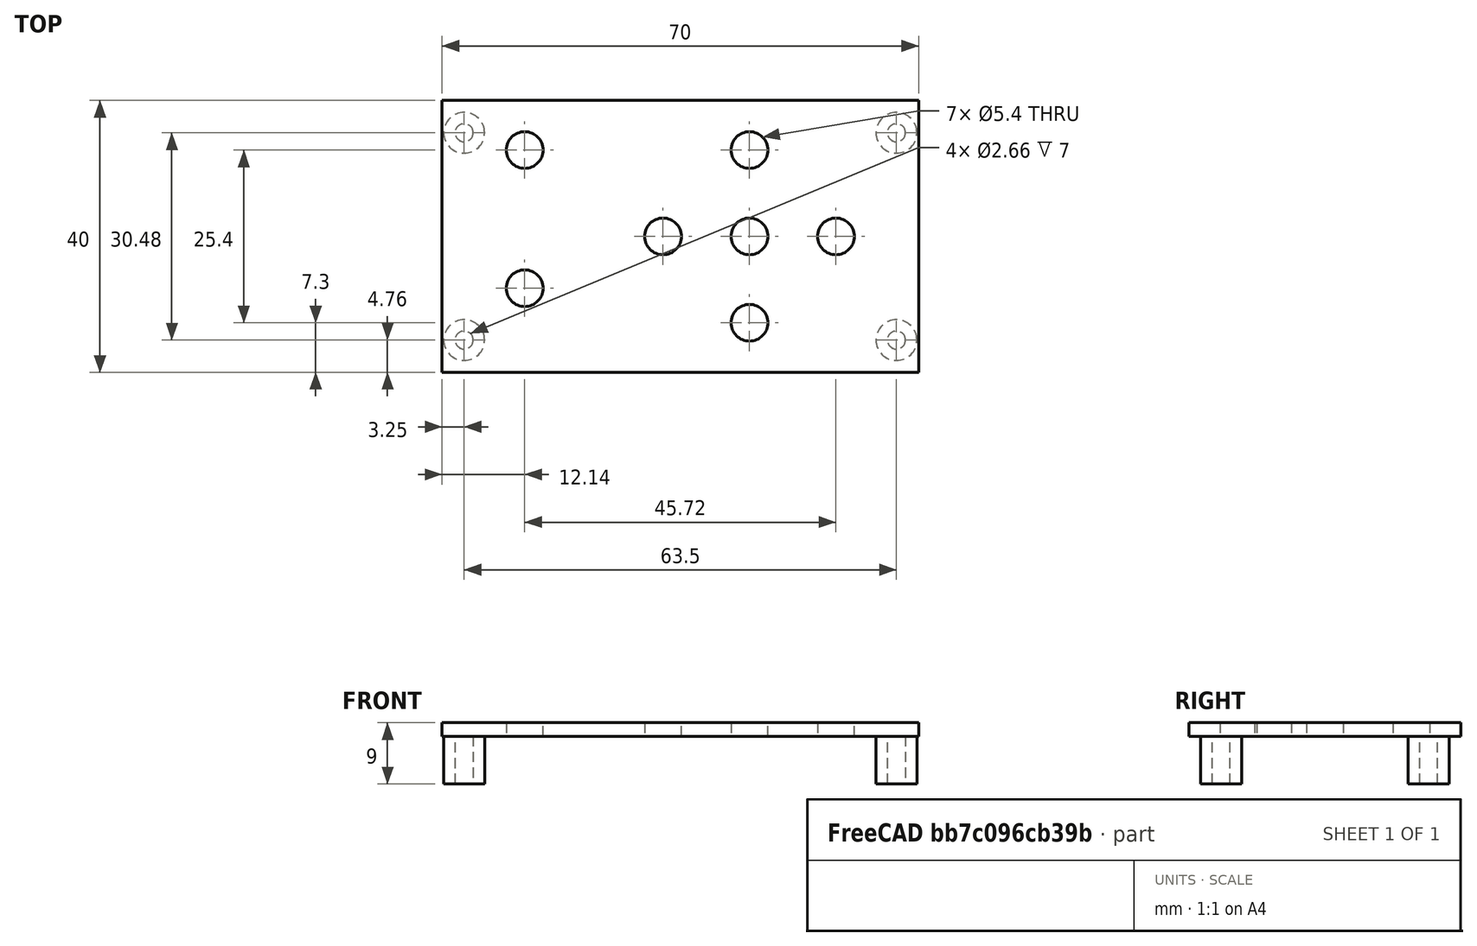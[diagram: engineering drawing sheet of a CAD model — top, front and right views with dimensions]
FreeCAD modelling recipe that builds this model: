
FCSTD DOCUMENT  (FreeCAD 0.17R13541 (Git))
Label: Frontplatte
License: CreativeCommons Attribution-NonCommercial-ShareAlike
LicenseURL: http://creativecommons.org/licenses/by-nc-sa/4.0/
objects: Sketcher::SketchObject×2, PartDesign::Pad×2, PartDesign::Body×1, Mesh::Feature×1
note: 7 computed .brp shape members not serialized (recipe doc carries the construction recipe); baked Part::Feature solids carry a one-line shape summary decoded from their .brp

FEATURE [Sketcher::SketchObject] Sketch
  MapMode = 5
  Support = -> [XY_Plane]
  sketch-geometry (15):
    g0: Circle CenterX=0 CenterY=0 CenterZ=0 NormalX=0 NormalY=0 NormalZ=1 AngleXU=0 Radius=2.7
    g1: Circle CenterX=0 CenterY=12.7 CenterZ=0 NormalX=0 NormalY=0 NormalZ=1 AngleXU=0 Radius=2.7
    g2: Circle CenterX=12.7 CenterY=0 CenterZ=0 NormalX=0 NormalY=0 NormalZ=1 AngleXU=0 Radius=2.7
    g3: Circle CenterX=-12.7 CenterY=0 CenterZ=0 NormalX=0 NormalY=0 NormalZ=1 AngleXU=0 Radius=2.7
    g4: Circle CenterX=0 CenterY=-12.7 CenterZ=0 NormalX=0 NormalY=0 NormalZ=1 AngleXU=0 Radius=2.7
    g5: Circle CenterX=-33.02 CenterY=12.7 CenterZ=0 NormalX=0 NormalY=0 NormalZ=1 AngleXU=0 Radius=2.7
    g6: Circle CenterX=-33.02 CenterY=-7.62 CenterZ=0 NormalX=0 NormalY=0 NormalZ=1 AngleXU=0 Radius=2.7
    g7: LineSegment [constr] StartX=-33.02 StartY=12.7 StartZ=0 EndX=-33.02 EndY=-7.62 EndZ=0
    g8: LineSegment [constr] StartX=0 StartY=12.7 StartZ=0 EndX=-33.02 EndY=12.7 EndZ=0
    g9: LineSegment StartX=-45.16 StartY=20 StartZ=0 EndX=24.84 EndY=20 EndZ=0
    g10: LineSegment StartX=24.84 StartY=20 StartZ=0 EndX=24.84 EndY=-20 EndZ=0
    g11: LineSegment StartX=24.84 StartY=-20 StartZ=0 EndX=-45.16 EndY=-20 EndZ=0
    g12: LineSegment StartX=-45.16 StartY=-20 StartZ=0 EndX=-45.16 EndY=20 EndZ=0
    g13: LineSegment [constr] StartX=-33.02 StartY=12.7 StartZ=0 EndX=-45.16 EndY=12.7 EndZ=0
    g14: LineSegment [constr] StartX=12.7 StartY=0 StartZ=0 EndX=24.84 EndY=0 EndZ=0
  constraints (42):
    c: Coincident(g0,g-1)
    c: PointOnObject(g1,g-2)
    c: PointOnObject(g4,g-2)
    c: PointOnObject(g2,g-1)
    c: PointOnObject(g3,g-1)
    c: Symmetric(g2,g3,g-2)
    c: Symmetric(g1,g4,g-1)
    c: DistanceX(g3,g2) = 25.4
    c: DistanceY(g4,g1) = 25.4
    c: Coincident(g7,g5)
    c: Coincident(g7,g6)
    c: Vertical(g7)
    c: Coincident(g8,g1)
    c: Coincident(g8,g5)
    c: Horizontal(g8)
    c: DistanceY(g7,g7) = 20.32
    c: DistanceX(g6,g3) = 20.32
    c: Radius(g0) = 2.7
    c: Equal(g0,g2)
    c: Equal(g0,g1)
    c: Equal(g0,g5)
    c: Equal(g0,g6)
    c: Equal(g0,g3)
    c: Equal(g0,g4)
    c: Coincident(g9,g10)
    c: Coincident(g10,g11)
    c: Coincident(g11,g12)
    c: Coincident(g12,g9)
    c: Horizontal(g9)
    c: Horizontal(g11)
    c: Vertical(g10)
    c: Vertical(g12)
    c: Coincident(g13,g5)
    c: PointOnObject(g13,g12)
    c: Horizontal(g13)
    c: Coincident(g14,g2)
    c: PointOnObject(g14,g10)
    c: Horizontal(g14)
    c: Equal(g14,g13)
    c: DistanceX(g11,g11) = 70
    c: DistanceY(g10,g10) = 40
    c: Symmetric(g9,g11,g-1)
FEATURE [PartDesign::Pad] Pad
  Length = 2
  Length2 = 100
  Profile = -> Sketch
  Refine = true
  Type = 0
FEATURE [Sketcher::SketchObject] Sketch001
  ExternalGeometry = -> [Pad]
  MapMode = 5
  Placement = pos=(0,0,0) rot=(1,0,0;3.14159rad)
  Support = -> [Pad]
  sketch-geometry (9):
    g0: Circle CenterX=-41.91 CenterY=15.24 CenterZ=0 NormalX=0 NormalY=0 NormalZ=1 AngleXU=0 Radius=3
    g1: Circle CenterX=21.59 CenterY=15.24 CenterZ=0 NormalX=0 NormalY=0 NormalZ=1 AngleXU=0 Radius=3
    g2: Circle CenterX=21.59 CenterY=-15.24 CenterZ=0 NormalX=0 NormalY=0 NormalZ=1 AngleXU=0 Radius=3
    g3: Circle CenterX=-41.91 CenterY=-15.24 CenterZ=0 NormalX=0 NormalY=0 NormalZ=1 AngleXU=0 Radius=3
    g4: LineSegment [constr] StartX=-10.16 StartY=20 StartZ=0 EndX=-10.16 EndY=-20 EndZ=0
    g5: Circle CenterX=-41.91 CenterY=15.24 CenterZ=0 NormalX=0 NormalY=0 NormalZ=1 AngleXU=0 Radius=1.33
    g6: Circle CenterX=21.59 CenterY=15.24 CenterZ=0 NormalX=0 NormalY=0 NormalZ=1 AngleXU=0 Radius=1.33
    g7: Circle CenterX=21.59 CenterY=-15.24 CenterZ=0 NormalX=0 NormalY=0 NormalZ=1 AngleXU=0 Radius=1.33
    g8: Circle CenterX=-41.91 CenterY=-15.24 CenterZ=0 NormalX=0 NormalY=0 NormalZ=1 AngleXU=0 Radius=1.33
  constraints (20):
    c: Symmetric(g4,g4,g-1)
    c: Equal(g-4,g4)
    c: Symmetric(g-3,g-4,g4)
    c: Symmetric(g0,g1,g4)
    c: Symmetric(g2,g3,g4)
    c: Symmetric(g3,g0,g-1)
    c: DistanceX(g0,g1) = 63.5
    c: Radius(g3) = 3
    c: Equal(g3,g0)
    c: Equal(g3,g1)
    c: Equal(g3,g2)
    c: DistanceY(g3,g0) = 30.48
    c: Coincident(g5,g0)
    c: Coincident(g6,g1)
    c: Coincident(g7,g2)
    c: Coincident(g8,g3)
    c: Radius(g8) = 1.33
    c: Equal(g8,g5)
    c: Equal(g8,g6)
    c: Equal(g8,g7)
FEATURE [PartDesign::Pad] Pad001
  BaseFeature = -> Pad
  Length = 7
  Length2 = 100
  Profile = -> Sketch001
  Refine = true
  Type = 0
FEATURE [PartDesign::Body] Body
  Group = -> [Sketch,Pad,Sketch001,Pad001]
  Origin = -> Origin
  Tip = -> Pad001
FEATURE [Mesh::Feature] Mesh  label="Body (Meshed)"
